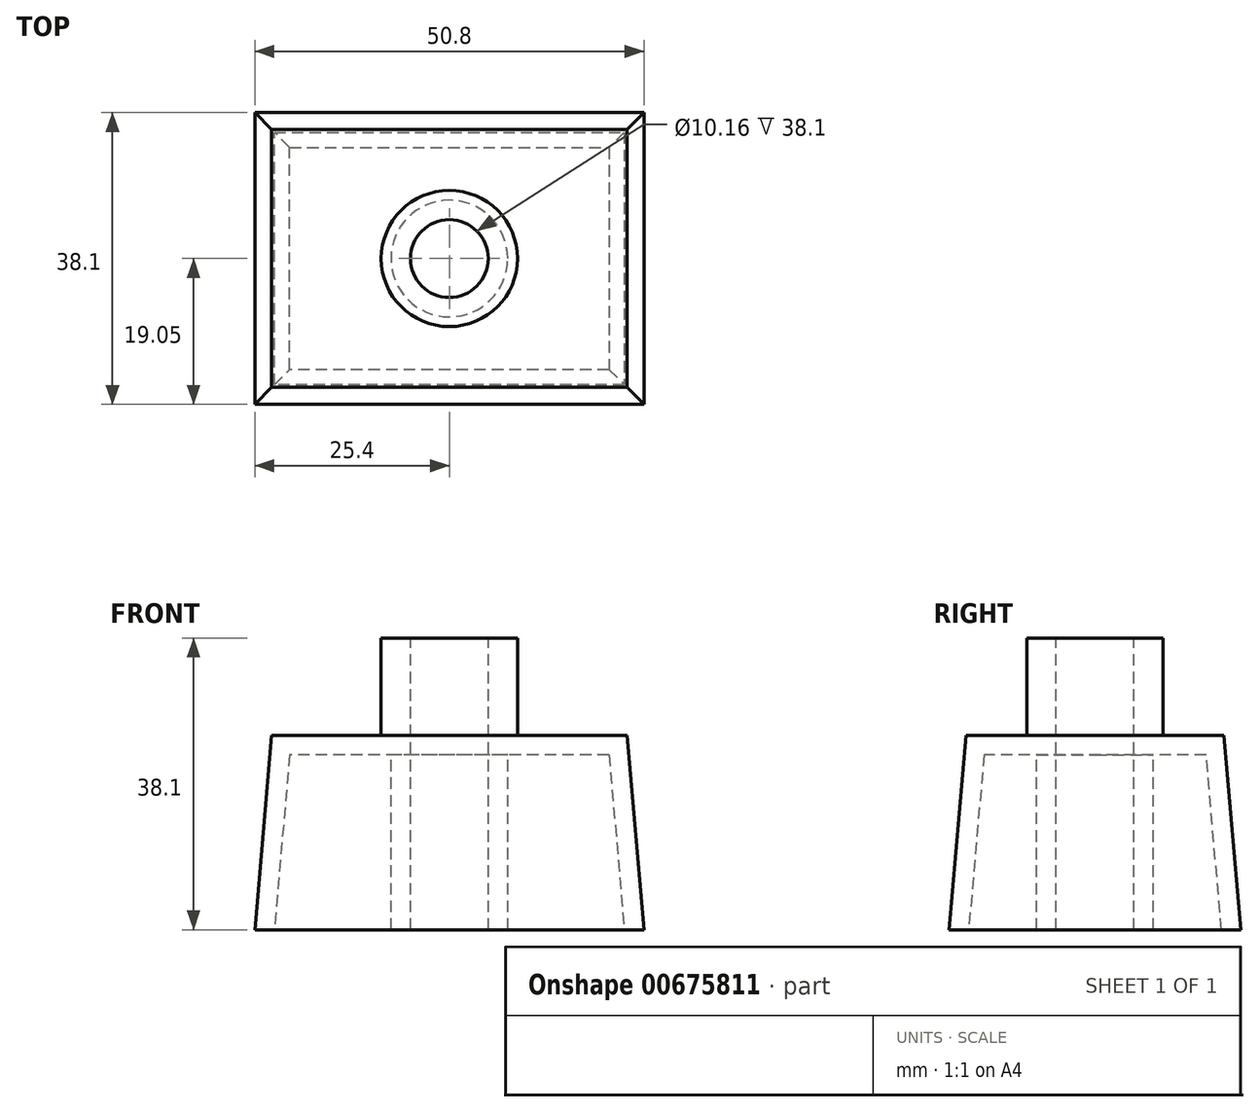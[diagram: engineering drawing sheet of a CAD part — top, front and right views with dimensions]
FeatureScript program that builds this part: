
annotation { "Feature Type Name" : "Feature", "Feature Type Description" : "" }
export const myFeature = defineFeature(function(context is Context, id is Id, definition is map)
    precondition{}
    {
        {
            var Q0;
            Q0=qCreatedBy(makeId("Top.planeOp"),FACE);
            var sketch = newSketch(context, id + "F0", { "sketchPlane" : qUnion([Q0])});
            skLineSegment(sketch, "E0.bottom", {"start": v(25.4, 19.05) * mm, "end": v(-25.4, 19.05) * mm});
            skLineSegment(sketch, "E0.top", {"start": v(25.4, -19.05) * mm, "end": v(-25.4, -19.05) * mm});
            skLineSegment(sketch, "E0.left", {"start": v(25.4, 19.05) * mm, "end": v(25.4, -19.05) * mm});
            skLineSegment(sketch, "E0.right", {"start": v(-25.4, 19.05) * mm, "end": v(-25.4, -19.05) * mm});
            skPoint(sketch, "E0.middle", {"position": v(0, 0) * mm});
            skSolve(sketch);
        }
        {
            var Q0;
            Q0 = qSketchRegion(id + "F0", true);
            extrude(context, id + "F1", {"entities" : qUnion([Q0]), "depth" : 25.4 * mm, "offsetDistance" : 25.4 * mm, "hasDraft" : true, "draftAngle" : 5 * degree, "draftPullDirection" : true});
        }
        {
            var Q0;
            Q0=makeQuery(id+"F1.opExtrude","CAP_FACE",FACE,{"disambiguationData":[OSD([sQuery(id+"F0.wireOp",EDGE,"E0.bottom"),sQuery(id+"F0.wireOp",EDGE,"E0.top"),sQuery(id+"F0.wireOp",EDGE,"E0.left"),sQuery(id+"F0.wireOp",EDGE,"E0.right")])],"isStart":false});
            var sketch = newSketch(context, id + "F2", { "sketchPlane" : qUnion([Q0])});
            skCircle(sketch, "E1", {"center": v(0, 0) * mm, "radius": 8.9 * mm});
            skSolve(sketch);
        }
        {
            var Q0;
            Q0 = qSketchRegion(id + "F2", true);
            extrude(context, id + "F3", {"entities" : qUnion([Q0]), "operationType" : NewBodyOperationType.ADD, "depth" : 12.7 * mm, "offsetDistance" : 25.4 * mm});
        }
        {
            var Q0;
            Q0=makeQuery(id+"F3.opExtrude","CAP_FACE",FACE,{"disambiguationData":[OSD([sQuery(id+"F2.wireOp",EDGE,"E1")])],"isStart":false});
            var sketch = newSketch(context, id + "F4", { "sketchPlane" : qUnion([Q0])});
            skCircle(sketch, "E2", {"center": v(0, 0) * mm, "radius": 5.08 * mm});
            skSolve(sketch);
        }
        {
            var Q0;
            Q0 = qSketchRegion(id + "F4", true);
            extrude(context, id + "F5", {"entities" : qUnion([Q0]), "operationType" : NewBodyOperationType.REMOVE, "endBound" : BoundingType.THROUGH_ALL, "oppositeDirection" : true, "depth" : 25.4 * mm, "offsetDistance" : 25.4 * mm});
        }
        {
            var Q0;
            Q0=makeQuery(id+"F1.opExtrude","CAP_FACE",FACE,{"disambiguationData":[OSD([sQuery(id+"F0.wireOp",EDGE,"E0.bottom"),sQuery(id+"F0.wireOp",EDGE,"E0.top"),sQuery(id+"F0.wireOp",EDGE,"E0.left"),sQuery(id+"F0.wireOp",EDGE,"E0.right")])],"isStart":true});
            shell(context, id + "F6", {"entities" : qUnion([Q0]), "thickness" : 2.54 * mm});
        }
    });
